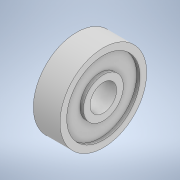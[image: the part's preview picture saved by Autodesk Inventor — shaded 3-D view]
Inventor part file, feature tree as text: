
AUTODESK INVENTOR PART (.ipt)
format: ipt  version: 2020 (Build 240168000, 168)  size: 128,512 bytes
history: native  units: mm
features: extrude x2, other x1, sketch x1
ambient origin geometry x8: Origin, YZ Plane, XZ Plane, XY Plane, X Axis, Y Axis, Z Axis, Center Point
bodies: Body1 (feature_tree)
feature tree (4):
  other  "Твердое тело1"
  sketch  "Эскиз1"
  extrude  "Выдавливание1"  Depth=4.0mm
  extrude  "Выдавливание2"  Depth=13.0mm
